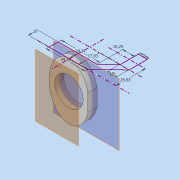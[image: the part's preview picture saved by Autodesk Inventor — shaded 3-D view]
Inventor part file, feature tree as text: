
AUTODESK INVENTOR PART (.ipt)
format: ipt  version: 2019 (Build 230136000, 136)  size: 125,952 bytes
history: native  units: mm
features: other x2, extrude x2, sketch x2
ambient origin geometry x8: Origin, YZ Plane, XZ Plane, XY Plane, X Axis, Y Axis, Z Axis, Center Point
bodies: Body1 (feature_tree)
feature tree (6):
  other  "Твердое тело1"
  extrude  "Выдавливание1"  Depth=34.31mm
  other  "РабПлоскость4"
  extrude  "Выдавливание2"  Depth=8.0mm
  sketch  "Эскиз1"
  sketch  "Эскиз7"
